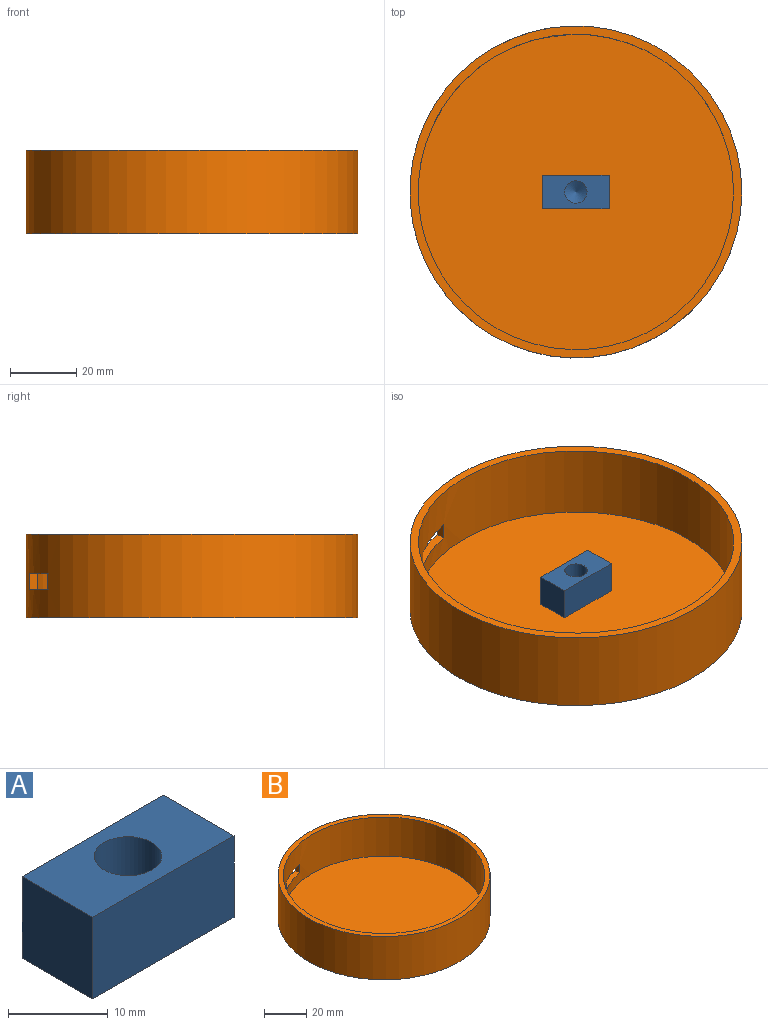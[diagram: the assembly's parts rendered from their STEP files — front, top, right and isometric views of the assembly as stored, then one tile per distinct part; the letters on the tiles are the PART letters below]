
ASSEMBLY  parts=2 mates=1
PART A: 8 faces, bbox 20x10x10 mm
  f0: plane 20x10mm, normal (0,-1,0), area 200mm2, adj f1,f3,f4,f5
  f1: plane 10x10mm, normal (1,0,0), area 100mm2, adj f0,f2,f4,f5
  f2: plane 20x10mm, normal (0,1,0), area 200mm2, adj f1,f3,f4,f5
  f3: plane 10x10mm, normal (-1,0,0), area 100mm2, adj f0,f2,f4,f5
  f4: plane 20x10mm, normal (0,0,1), area 164.1mm2, adj f0,f1,f2,f3,f7
  f5: plane 20x10mm, normal (0,0,-1), area 200mm2, adj f0,f1,f2,f3
  f6: cone r=0mm half-angle=59deg, axis (0,0,1), area 41.8mm2, adj f7
  f7: cylinder r=3.38mm len=6.76mm, axis (0,0,1), area 106.1mm2, adj f4,f6
PART B: 9 faces, bbox 100x100x25 mm
  f0: cylinder r=50mm len=100mm, axis (0,0,-1), area 7777.3mm2, adj f2,f3,f5,f6,f7,f8
  f1: cylinder r=47.5mm len=95mm, axis (0,0,-1), area 6637.9mm2, adj f2,f4,f5,f6,f7,f8
  f2: plane 100x100mm, normal (0,0,1), area 765.8mm2, adj f0,f1
  f3: plane 100x100mm, normal (0,0,-1), area 7854mm2, adj f0
  f4: plane 95x95mm, normal (0,0,1), area 7088.2mm2, adj f1
  f5: plane 14.64x8.41mm, normal (0,0,-1), area 39.4mm2, adj f0,f1,f6,f8
  f6: plane 4.88x2.9mm, normal (1,0,0), area 14.2mm2, adj f0,f1,f5,f7
  f7: plane 14.64x8.41mm, normal (0,0,1), area 39.4mm2, adj f0,f1,f6,f8
  f8: plane 4.88x2.56mm, normal (-1,0,0), area 12.5mm2, adj f0,f1,f5,f7
PLACE A t=(0.05,0.07,-7.98)mm
PLACE B t=(0.05,0.07,-12.51)mm fixed
MATE fastened A.f6 <-> B.f0  axis (0,0,1) through (0.05,0.07,-5.01)mm
